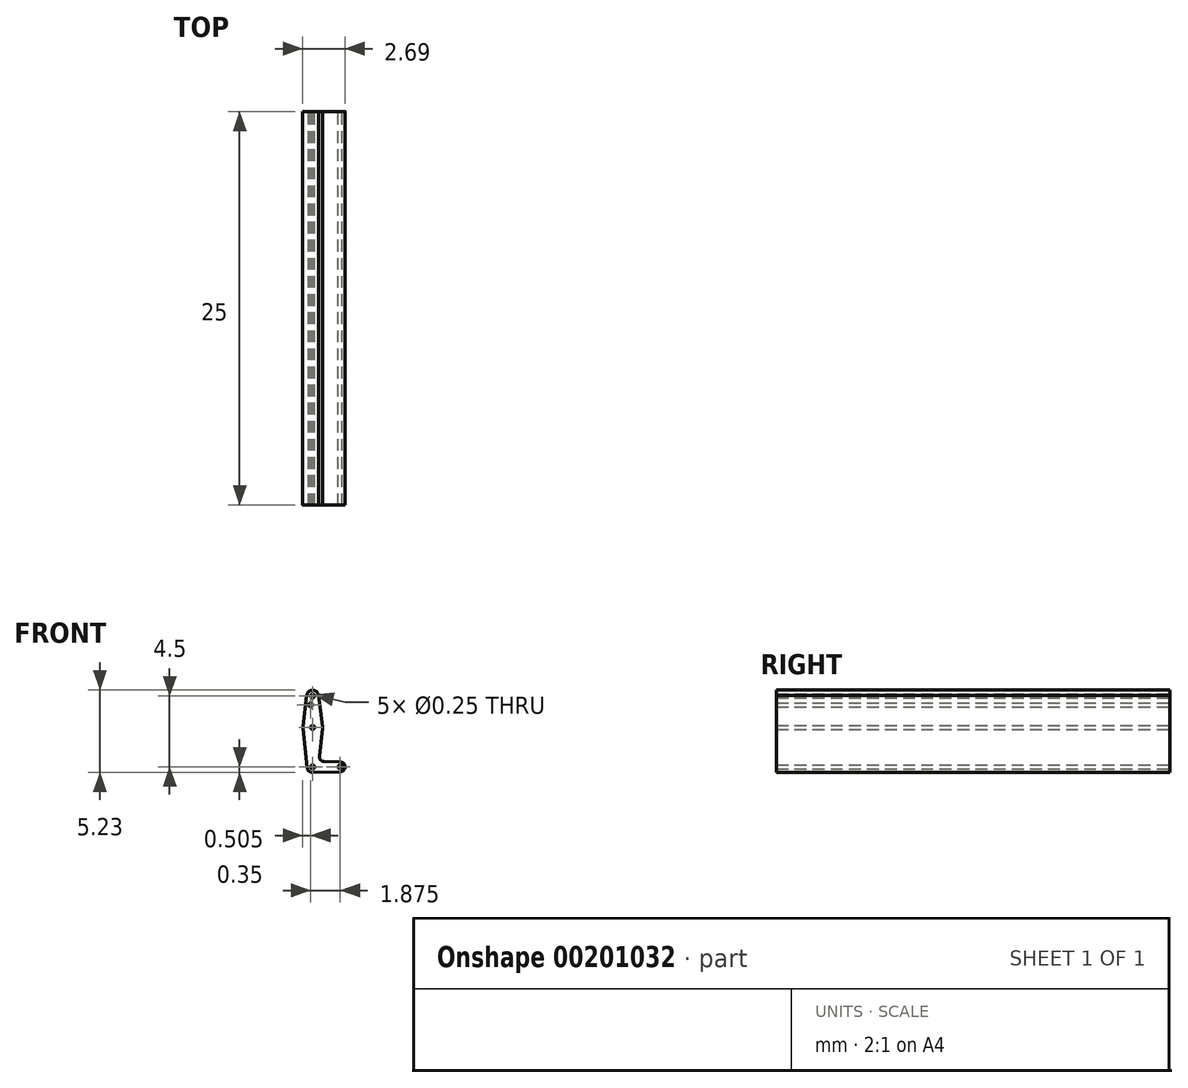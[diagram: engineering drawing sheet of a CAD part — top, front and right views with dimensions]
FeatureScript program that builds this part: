
annotation { "Feature Type Name" : "Feature", "Feature Type Description" : "" }
export const myFeature = defineFeature(function(context is Context, id is Id, definition is map)
    precondition{}
    {
        {
            var Q0;
            Q0=qCreatedBy(makeId("Front.planeOp"),FACE);
            var sketch = newSketch(context, id + "F0", { "sketchPlane" : qUnion([Q0])});
            skLineSegment(sketch, "E0", {"start": v(0, 4.5) * mm, "end": v(0, 0) * mm, "construction": true});
            skLineSegment(sketch, "E1", {"start": v(0, 0) * mm, "end": v(1.75, 0) * mm, "construction": true});
            skCircle(sketch, "E2", {"center": v(0, 4.5) * mm, "radius": 0.38 * mm});
            skCircle(sketch, "E3", {"center": v(0, 2.5) * mm, "radius": 0.62 * mm});
            skCircle(sketch, "E4", {"center": v(0, 0) * mm, "radius": 0.35 * mm});
            skCircle(sketch, "E5", {"center": v(1.75, 0) * mm, "radius": 0.31 * mm});
            skLineSegment(sketch, "E6", {"start": v(-0.37, 4.55) * mm, "end": v(-0.62, 2.58) * mm});
            skLineSegment(sketch, "E7", {"start": v(0.37, 4.54) * mm, "end": v(0.62, 2.58) * mm});
            skLineSegment(sketch, "E8", {"start": v(-0.62, 2.43) * mm, "end": v(-0.35, -0.04) * mm});
            skLineSegment(sketch, "E9", {"start": v(0.62, 2.43) * mm, "end": v(0.43, 0.68) * mm});
            skLineSegment(sketch, "E10", {"start": v(0.73, 0.34) * mm, "end": v(1.76, 0.31) * mm});
            skLineSegment(sketch, "E11", {"start": v(1.76, -0.31) * mm, "end": v(0, -0.35) * mm});
            skCircle(sketch, "E12", {"center": v(0, 4.5) * mm, "radius": 0.12 * mm});
            skCircle(sketch, "E13", {"center": v(0, 2.5) * mm, "radius": 0.12 * mm});
            skCircle(sketch, "E14", {"center": v(0, 0) * mm, "radius": 0.12 * mm});
            skCircle(sketch, "E15", {"center": v(1.75, 0) * mm, "radius": 0.12 * mm});
            skCircle(sketch, "E16", {"center": v(-0.13, 3.94) * mm, "radius": 0.12 * mm});
            skPoint(sketch, "E17.newPointB", {"position": v(0.35, -0.04) * mm});
            skArc(sketch, "E17.filletArc", {"start": v(0.43, 0.68) * mm, "mid": v(0.5, 0.44) * mm, "end": v(0.73, 0.34) * mm});
            skSolve(sketch);
        }
        {
            var Q0;
            Q0 = qSketchRegion(id + "F0", true);
            extrude(context, id + "F1", {"entities" : qUnion([Q0]), "depth" : 25 * mm});
        }
    });
